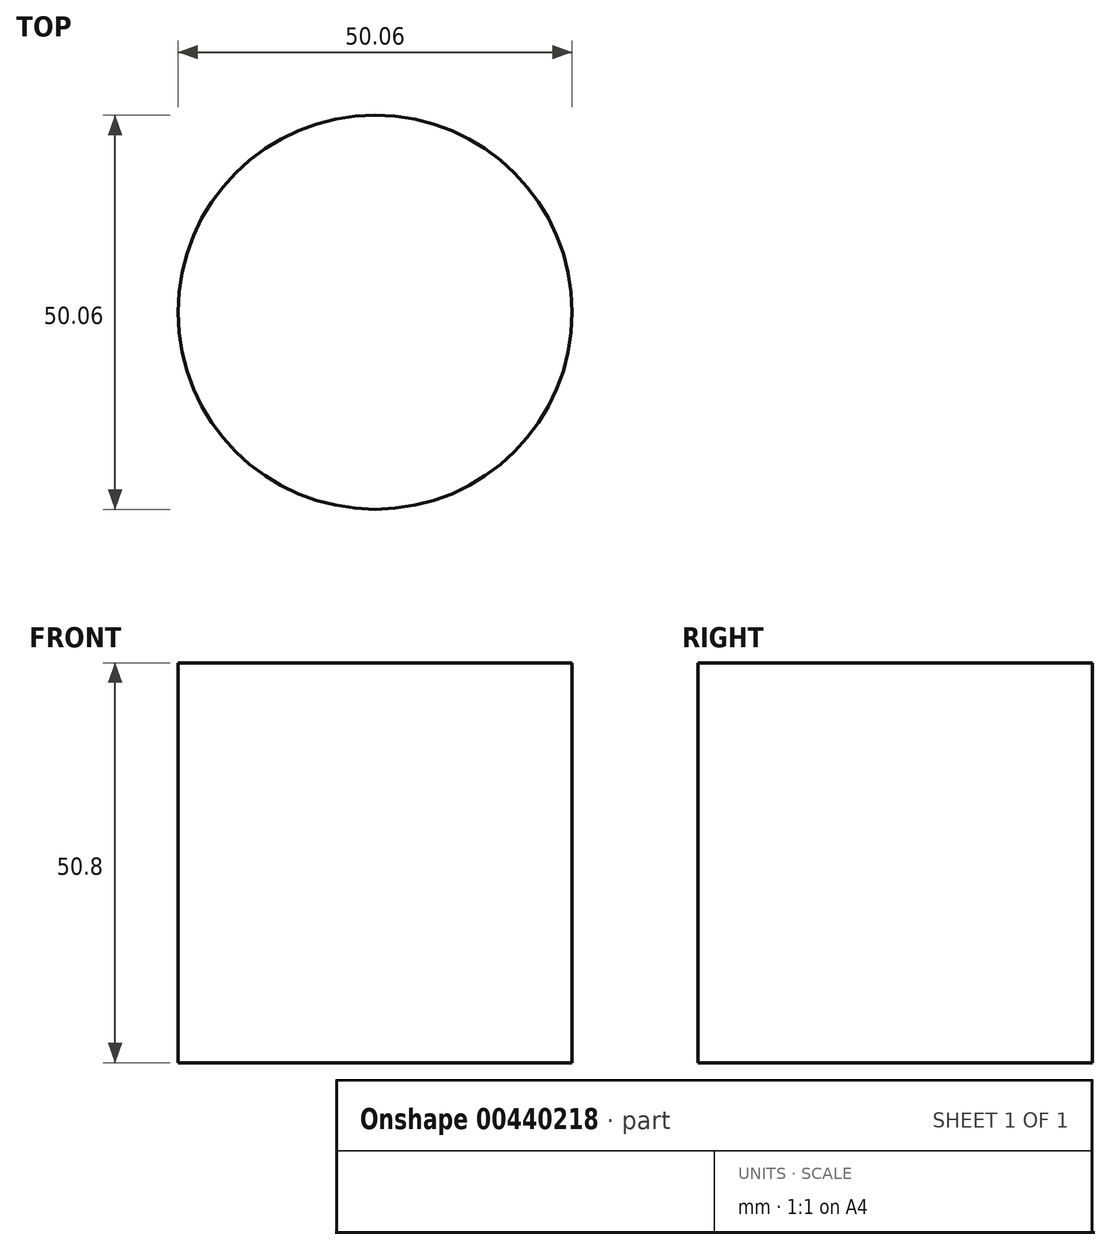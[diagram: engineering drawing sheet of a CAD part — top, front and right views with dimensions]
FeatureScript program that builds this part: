
annotation { "Feature Type Name" : "Feature", "Feature Type Description" : "" }
export const myFeature = defineFeature(function(context is Context, id is Id, definition is map)
    precondition{}
    {
        {
            var Q0;
            Q0=qCreatedBy(makeId("Top.planeOp"),FACE);
            var sketch = newSketch(context, id + "F0", { "sketchPlane" : qUnion([Q0])});
            skCircle(sketch, "E0", {"center": v(0, 0) * mm, "radius": 25.03 * mm});
            skSolve(sketch);
        }
        {
            var Q0;
            Q0=makeQuery(id+"F0.imprint","IMPRINT",FACE,{"disambiguationData":[TD([[makeQuery(id+"F0.imprint","IMPRINT",EDGE,{"derivedFrom":sQuery(id+"F0.wireOp",EDGE,"E0")}),1.0]])]});
            extrude(context, id + "F1", {"entities" : qUnion([Q0]), "depth" : 50.8 * mm});
        }
    });
